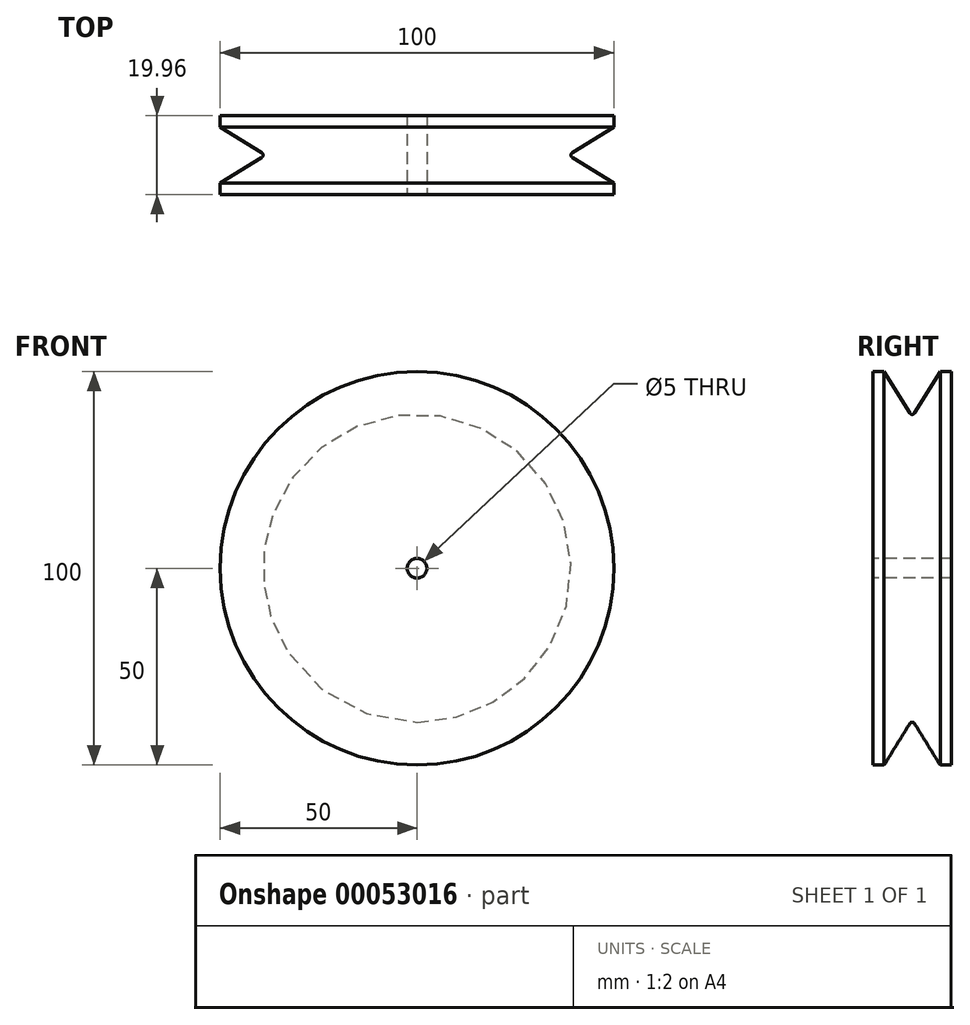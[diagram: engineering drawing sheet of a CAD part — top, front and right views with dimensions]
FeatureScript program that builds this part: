
annotation { "Feature Type Name" : "Feature", "Feature Type Description" : "" }
export const myFeature = defineFeature(function(context is Context, id is Id, definition is map)
    precondition{}
    {
        {
            var Q0;
            Q0=qCreatedBy(makeId("Right.planeOp"),FACE);
            var sketch = newSketch(context, id + "F0", { "sketchPlane" : qUnion([Q0])});
            skLineSegment(sketch, "E0", {"start": v(0, 0) * mm, "end": v(0, 50) * mm});
            skLineSegment(sketch, "E1", {"start": v(0, 50) * mm, "end": v(-2.85, 50) * mm});
            skLineSegment(sketch, "E2", {"start": v(-2.85, 50) * mm, "end": v(-9.38, 39.44) * mm});
            skLineSegment(sketch, "E3", {"start": v(-10.58, 39.44) * mm, "end": v(-17.1, 50) * mm});
            skLineSegment(sketch, "E4", {"start": v(-17.1, 50) * mm, "end": v(-19.96, 50) * mm});
            skLineSegment(sketch, "E5", {"start": v(-19.96, 50) * mm, "end": v(-19.96, 0) * mm});
            skLineSegment(sketch, "E6", {"start": v(-19.96, 0) * mm, "end": v(0.04, 0) * mm});
            skPoint(sketch, "E7.visualSharp", {"position": v(-9.98, 38.47) * mm});
            skArc(sketch, "E7.filletArc", {"start": v(-10.58, 39.44) * mm, "mid": v(-9.98, 39.1) * mm, "end": v(-9.38, 39.44) * mm});
            skSolve(sketch);
        }
        {
            var Q0;
            {var subQ0=sQuery(id+"F0.wireOp",EDGE,"E0");Q0=makeQuery(id+"F0.imprint","IMPRINT",FACE,{"disambiguationData":[TD([[makeQuery(id+"F0.imprint","IMPRINT",EDGE,{"derivedFrom":subQ0}),1.0]])]});}
            var Q1;
            Q1=sQuery(id+"F0.wireOp",EDGE,"E6");
            revolve(context, id + "F1", {"entities" : qUnion([Q0]), "axis" : qUnion([Q1]), "revolveType" : RevolveType.FULL});
        }
        {
            var Q0;
            Q0=makeQuery(id+"F1.opRevolve","SWEPT_FACE",FACE,{"disambiguationData":[OSD([sQuery(id+"F0.wireOp",EDGE,"E5")])]});
            var sketch = newSketch(context, id + "F2", { "sketchPlane" : qUnion([Q0])});
            skCircle(sketch, "E8", {"center": v(0, 0) * mm, "radius": 2.5 * mm});
            skSolve(sketch);
        }
        {
            var Q0;
            Q0=makeQuery(id+"F2.imprint","IMPRINT",FACE,{"disambiguationData":[TD([[makeQuery(id+"F2.imprint","IMPRINT",EDGE,{"derivedFrom":sQuery(id+"F2.wireOp",EDGE,"E8")}),1.0]])]});
            extrude(context, id + "F3", {"entities" : qUnion([Q0]), "operationType" : NewBodyOperationType.REMOVE, "endBound" : BoundingType.THROUGH_ALL, "oppositeDirection" : true, "depth" : 25 * mm});
        }
    });
